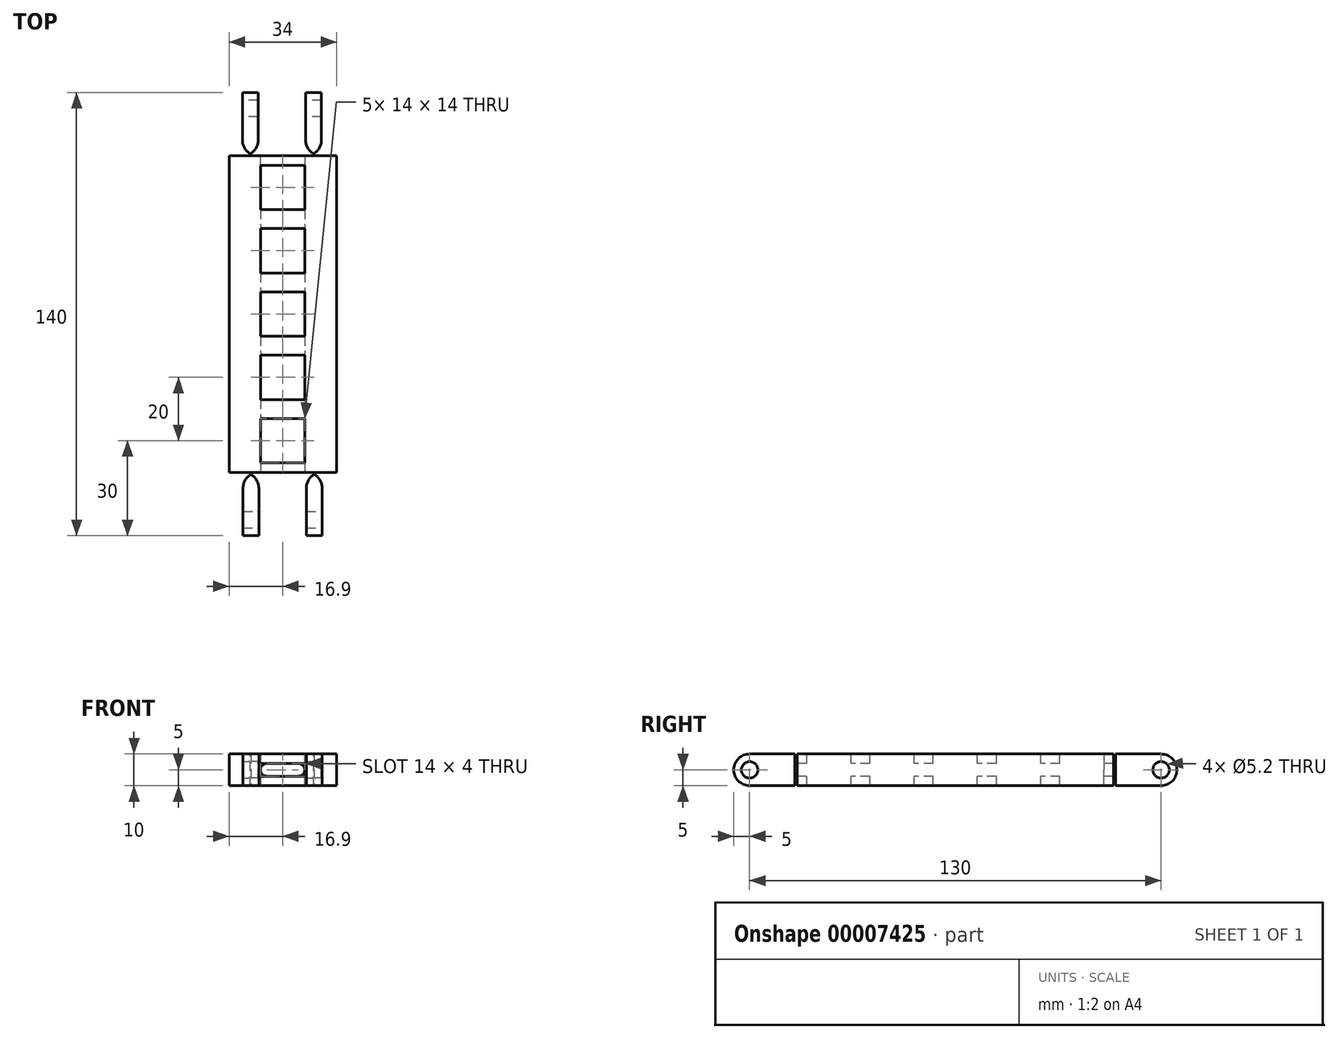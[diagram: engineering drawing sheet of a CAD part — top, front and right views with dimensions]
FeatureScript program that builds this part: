
annotation { "Feature Type Name" : "Feature", "Feature Type Description" : "" }
export const myFeature = defineFeature(function(context is Context, id is Id, definition is map)
    precondition{}
    {
        {
            var Q0;
            Q0=qCreatedBy(makeId("Top.planeOp"),FACE);
            var sketch = newSketch(context, id + "F0", { "sketchPlane" : qUnion([Q0])});
            skLineSegment(sketch, "E0.rect.bottom", {"start": v(17, 50) * mm, "end": v(-17, 50) * mm});
            skLineSegment(sketch, "E0.rect.top", {"start": v(17, -50) * mm, "end": v(-17, -50) * mm});
            skLineSegment(sketch, "E0.rect.left", {"start": v(17, 50) * mm, "end": v(17, -50) * mm});
            skLineSegment(sketch, "E0.rect.right", {"start": v(-17, 50) * mm, "end": v(-17, -50) * mm});
            skPoint(sketch, "E0.rect.middle", {"position": v(0, 0) * mm});
            skLineSegment(sketch, "E1.0", {"start": v(14, 47) * mm, "end": v(14, -47) * mm});
            skLineSegment(sketch, "E1.1", {"start": v(14, 47) * mm, "end": v(-14, 47) * mm});
            skLineSegment(sketch, "E1.2", {"start": v(-14, 47) * mm, "end": v(-14, -47) * mm});
            skLineSegment(sketch, "E1.3", {"start": v(14, -47) * mm, "end": v(-14, -47) * mm});
            skSolve(sketch);
        }
        {
            var Q0;
            Q0=makeQuery(id+"F0.imprint","IMPRINT",FACE,{"disambiguationData":[TD([[makeQuery(id+"F0.imprint","IMPRINT",EDGE,{"derivedFrom":sQuery(id+"F0.wireOp",EDGE,"E0.rect.bottom")}),1.0]])]});
            extrude(context, id + "F1", {"entities" : qUnion([Q0]), "depth" : 10 * mm});
        }
        {
            var Q0;
            Q0=makeQuery(id+"F1.opExtrude","SWEPT_FACE",FACE,{"disambiguationData":[OSD([sQuery(id+"F0.wireOp",EDGE,"E0.rect.top")])]});
            var sketch = newSketch(context, id + "F2", { "sketchPlane" : qUnion([Q0])});
            skLineSegment(sketch, "E2.bottom", {"start": v(-12.6, 10) * mm, "end": v(-7.6, 10) * mm});
            skLineSegment(sketch, "E2.top", {"start": v(-12.6, 0) * mm, "end": v(-7.6, 0) * mm});
            skLineSegment(sketch, "E2.left", {"start": v(-12.6, 10) * mm, "end": v(-12.6, 0) * mm});
            skLineSegment(sketch, "E2.right", {"start": v(-7.6, 10) * mm, "end": v(-7.6, 0) * mm});
            skLineSegment(sketch, "E3", {"start": v(-17, 5) * mm, "end": v(-12.6, 5) * mm});
            skSolve(sketch);
        }
        {
            var Q0;
            {var subQ4=sQuery(id+"F2.wireOp",EDGE,"E2.bottom");Q0=makeQuery(id+"F2.imprint","IMPRINT",FACE,{"disambiguationData":[TD([[makeQuery(id+"F2.imprint","IMPRINT",EDGE,{"derivedFrom":subQ4}),1.0]])]});}
            var Q1;
            Q1=makeQuery(id+"F2.imprint","IMPRINT",FACE,{"disambiguationData":[TD([[makeQuery(id+"F2.imprint","IMPRINT",EDGE,{"derivedFrom":sQuery(id+"F2.wireOp",EDGE,"91248dbe-fa9f-4d01-a37b-5694f4a21cfa.0.MirrorCS")}),1.0]])]});
            extrude(context, id + "F3", {"entities" : qUnion([Q0, Q1]), "depth" : 15 * mm});
        }
        {
            var Q0;
            Q0=makeQuery(id+"F3.opExtrude","SWEPT_FACE",FACE,{"disambiguationData":[OSD([sQuery(id+"F2.wireOp",EDGE,"E2.right")])]});
            var sketch = newSketch(context, id + "F4", { "sketchPlane" : qUnion([Q0])});
            skCircle(sketch, "E4", {"center": v(-65, 5) * mm, "radius": 5 * mm});
            skSolve(sketch);
        }
        {
            var Q0;
            {var subQ0=sQuery(id+"F2.wireOp",EDGE,"E2.right");var subQ1=makeQuery(id+"F3.opExtrude","CAP_EDGE",EDGE,{"disambiguationData":[OSD([subQ0])],"isStart":false});Q0=makeQuery(id+"F4.imprint","IMPRINT",FACE,{"disambiguationData":[TD([[makeQuery(id+"F4.imprint","IMPRINT",EDGE,{"derivedFrom":subQ1}),-1.0]])]});}
            extrude(context, id + "F5", {"entities" : qUnion([Q0]), "oppositeDirection" : true, "depth" : 5 * mm});
        }
        {
            var Q0;
            Q0=makeQuery(id+"F5.opExtrude","SWEPT_BODY",BODY,{"disambiguationData":[OSD([sQuery(id+"F2.wireOp",EDGE,"E2.right"),sQuery(id+"F4.wireOp",EDGE,"E4")])]});
            var Q1;
            Q1=makeQuery(id+"F3.opExtrude","SWEPT_BODY",BODY,{"disambiguationData":[OSD([sQuery(id+"F2.wireOp",EDGE,"E2.bottom"),sQuery(id+"F2.wireOp",EDGE,"E2.top"),sQuery(id+"F2.wireOp",EDGE,"E2.left"),sQuery(id+"F2.wireOp",EDGE,"E2.right")])]});
            booleanBodies(context, id + "F6", {"operationType" : BooleanOperationType.UNION, "tools" : qUnion([Q0, Q1])});
        }
        {
            var Q0;
            {var subQ0=sQuery(id+"F2.wireOp",EDGE,"E2.right");Q0=makeQuery(id+"F6.opBoolean","MERGE",FACE,{"derivedFrom":[makeQuery(id+"F3.opExtrude","SWEPT_FACE",FACE,{"disambiguationData":[OSD([subQ0])]}),makeQuery(id+"F5.opExtrude","CAP_FACE",FACE,{"disambiguationData":[OSD([subQ0,sQuery(id+"F4.wireOp",EDGE,"E4")])],"isStart":true})]});}
            var sketch = newSketch(context, id + "F7", { "sketchPlane" : qUnion([Q0])});
            skLineSegment(sketch, "E5", {"start": v(-65, 10) * mm, "end": v(-65, 0) * mm});
            skCircle(sketch, "E6", {"center": v(-65, 5) * mm, "radius": 2.6 * mm});
            skSolve(sketch);
        }
        {
            var Q0;
            {var subQ0=sQuery(id+"F7.wireOp",EDGE,"E6");var subQ1=sQuery(id+"F7.wireOp",EDGE,"E5");var subQ3=makeQuery(id+"F7.imprint","INTERSECT",VERTEX,{"disambiguationData":[OD(0.0)],"derivedFrom":[subQ1,subQ0]});Q0=makeQuery(id+"F7.imprint","IMPRINT",FACE,{"disambiguationData":[TD([[makeQuery(id+"F7.imprint","IMPRINT",EDGE,{"disambiguationData":[TD([[subQ3,-1.0]])],"derivedFrom":subQ1}),1.0]])]});}
            var Q1;
            {var subQ0=sQuery(id+"F7.wireOp",EDGE,"E6");var subQ1=sQuery(id+"F7.wireOp",EDGE,"E5");var subQ3=makeQuery(id+"F7.imprint","INTERSECT",VERTEX,{"disambiguationData":[OD(0.0)],"derivedFrom":[subQ1,subQ0]});Q1=makeQuery(id+"F7.imprint","IMPRINT",FACE,{"disambiguationData":[TD([[makeQuery(id+"F7.imprint","IMPRINT",EDGE,{"disambiguationData":[TD([[subQ3,-1.0]])],"derivedFrom":subQ1}),-1.0]])]});}
            extrude(context, id + "F8", {"entities" : qUnion([Q0, Q1]), "operationType" : NewBodyOperationType.REMOVE, "endBound" : BoundingType.THROUGH_ALL, "oppositeDirection" : true, "depth" : 25 * mm});
        }
        {
            var Q0;
            Q0=makeQuery(id+"F5.opExtrude","SWEPT_BODY",BODY,{"disambiguationData":[OSD([sQuery(id+"F2.wireOp",EDGE,"E2.right"),sQuery(id+"F4.wireOp",EDGE,"E4")])]});
            transform(context, id + "F9", {"entities" : qUnion([Q0]), "transformType" : TransformType.TRANSLATION_3D, "dx" : 20 * mm, "dy" : 0 * mm, "dz" : 0 * mm, "makeCopy" : true});
        }
        {
            var Q0;
            Q0=makeQuery(id+"F5.opExtrude","SWEPT_BODY",BODY,{"disambiguationData":[OSD([sQuery(id+"F2.wireOp",EDGE,"E2.right"),sQuery(id+"F4.wireOp",EDGE,"E4")])]});
            var Q1;
            Q1=makeQuery(id+"F9.opPattern","COPY",BODY,{"derivedFrom":makeQuery(id+"F5.opExtrude","SWEPT_BODY",BODY,{"disambiguationData":[OSD([sQuery(id+"F2.wireOp",EDGE,"E2.right"),sQuery(id+"F4.wireOp",EDGE,"E4")])]}),"instanceName":"1"});
            transform(context, id + "F10", {"entities" : qUnion([Q0, Q1]), "transformType" : TransformType.TRANSLATION_3D, "dx" : -25.2 * mm, "dy" : 100 * mm, "dz" : 0 * mm, "makeCopy" : true});
        }
        {
            var Q0;
            Q0=makeQuery(id+"F10.opPattern","COPY",BODY,{"derivedFrom":makeQuery(id+"F5.opExtrude","SWEPT_BODY",BODY,{"disambiguationData":[OSD([sQuery(id+"F2.wireOp",EDGE,"E2.right"),sQuery(id+"F4.wireOp",EDGE,"E4")])]}),"instanceName":"1"});
            var Q1;
            Q1=makeQuery(id+"F10.opPattern","COPY",BODY,{"derivedFrom":makeQuery(id+"F9.opPattern","COPY",BODY,{"derivedFrom":makeQuery(id+"F5.opExtrude","SWEPT_BODY",BODY,{"disambiguationData":[OSD([sQuery(id+"F2.wireOp",EDGE,"E2.right"),sQuery(id+"F4.wireOp",EDGE,"E4")])]}),"instanceName":"1"}),"instanceName":"1"});
            var Q2;
            Q2=makeQuery(id+"F10.opPattern","COPY",EDGE,{"derivedFrom":makeQuery(id+"F9.opPattern","COPY",EDGE,{"derivedFrom":makeQuery(id+"F3.opExtrude","CAP_EDGE",EDGE,{"disambiguationData":[OSD([sQuery(id+"F2.wireOp",EDGE,"E2.right")])],"isStart":true}),"instanceName":"1"}),"instanceName":"1"});
            transform(context, id + "F11", {"entities" : qUnion([Q0, Q1]), "transformType" : TransformType.ROTATION, "transformAxis" : qUnion([Q2]), "angle" : 180 * degree, "makeCopy" : false});
        }
        {
            var Q0;
            Q0=makeQuery(id+"F1.opExtrude","SWEPT_FACE",FACE,{"disambiguationData":[OSD([sQuery(id+"F0.wireOp",EDGE,"E1.2")])]});
            var sketch = newSketch(context, id + "F12", { "sketchPlane" : qUnion([Q0])});
            skPoint(sketch, "E7", {"position": v(30, 10) * mm});
            skPoint(sketch, "E8", {"position": v(10, 10) * mm});
            skPoint(sketch, "E9", {"position": v(-10, 10) * mm});
            skPoint(sketch, "E10", {"position": v(-30, 10) * mm});
            skLineSegment(sketch, "E11", {"start": v(-30, 10) * mm, "end": v(-30, 0) * mm});
            skLineSegment(sketch, "E12", {"start": v(-10, 10) * mm, "end": v(-10, 0) * mm});
            skLineSegment(sketch, "E13", {"start": v(10, 10) * mm, "end": v(10, 0) * mm});
            skLineSegment(sketch, "E14", {"start": v(30, 10) * mm, "end": v(30, 0) * mm});
            skPoint(sketch, "E15", {"position": v(33, 10) * mm});
            skPoint(sketch, "E16", {"position": v(27, 10) * mm});
            skLineSegment(sketch, "E17", {"start": v(27, 10) * mm, "end": v(27, 0) * mm});
            skLineSegment(sketch, "E18", {"start": v(33, 10) * mm, "end": v(33, 0) * mm});
            skPoint(sketch, "E19", {"position": v(13, 10) * mm});
            skPoint(sketch, "E20", {"position": v(7, 10) * mm});
            skPoint(sketch, "E21", {"position": v(-7, 10) * mm});
            skPoint(sketch, "E22", {"position": v(-13, 10) * mm});
            skPoint(sketch, "E23", {"position": v(-27, 10) * mm});
            skPoint(sketch, "E24", {"position": v(-33, 10) * mm});
            skLineSegment(sketch, "E25", {"start": v(13, 10) * mm, "end": v(13, 0) * mm});
            skLineSegment(sketch, "E26", {"start": v(7, 10) * mm, "end": v(7, 0) * mm});
            skLineSegment(sketch, "E27", {"start": v(-7, 10) * mm, "end": v(-7, 0) * mm});
            skLineSegment(sketch, "E28", {"start": v(-13, 10) * mm, "end": v(-13, 0) * mm});
            skLineSegment(sketch, "E29", {"start": v(-27, 10) * mm, "end": v(-27, 0) * mm});
            skLineSegment(sketch, "E30", {"start": v(-33, 10) * mm, "end": v(-33, 0) * mm});
            skSolve(sketch);
        }
        {
            var Q0;
            {var subQ3=sQuery(id+"F12.wireOp",EDGE,"E11");Q0=makeQuery(id+"F12.imprint","IMPRINT",FACE,{"disambiguationData":[TD([[makeQuery(id+"F12.imprint","IMPRINT",EDGE,{"derivedFrom":subQ3}),-1.0]])]});}
            var Q1;
            {var subQ3=sQuery(id+"F12.wireOp",EDGE,"E11");Q1=makeQuery(id+"F12.imprint","IMPRINT",FACE,{"disambiguationData":[TD([[makeQuery(id+"F12.imprint","IMPRINT",EDGE,{"derivedFrom":subQ3}),1.0]])]});}
            var Q2;
            {var subQ3=sQuery(id+"F12.wireOp",EDGE,"E12");Q2=makeQuery(id+"F12.imprint","IMPRINT",FACE,{"disambiguationData":[TD([[makeQuery(id+"F12.imprint","IMPRINT",EDGE,{"derivedFrom":subQ3}),-1.0]])]});}
            var Q3;
            {var subQ3=sQuery(id+"F12.wireOp",EDGE,"E12");Q3=makeQuery(id+"F12.imprint","IMPRINT",FACE,{"disambiguationData":[TD([[makeQuery(id+"F12.imprint","IMPRINT",EDGE,{"derivedFrom":subQ3}),1.0]])]});}
            var Q4;
            {var subQ3=sQuery(id+"F12.wireOp",EDGE,"E13");Q4=makeQuery(id+"F12.imprint","IMPRINT",FACE,{"disambiguationData":[TD([[makeQuery(id+"F12.imprint","IMPRINT",EDGE,{"derivedFrom":subQ3}),-1.0]])]});}
            var Q5;
            {var subQ3=sQuery(id+"F12.wireOp",EDGE,"E13");Q5=makeQuery(id+"F12.imprint","IMPRINT",FACE,{"disambiguationData":[TD([[makeQuery(id+"F12.imprint","IMPRINT",EDGE,{"derivedFrom":subQ3}),1.0]])]});}
            var Q6;
            {var subQ3=sQuery(id+"F12.wireOp",EDGE,"E14");Q6=makeQuery(id+"F12.imprint","IMPRINT",FACE,{"disambiguationData":[TD([[makeQuery(id+"F12.imprint","IMPRINT",EDGE,{"derivedFrom":subQ3}),-1.0]])]});}
            var Q7;
            {var subQ3=sQuery(id+"F12.wireOp",EDGE,"E14");Q7=makeQuery(id+"F12.imprint","IMPRINT",FACE,{"disambiguationData":[TD([[makeQuery(id+"F12.imprint","IMPRINT",EDGE,{"derivedFrom":subQ3}),1.0]])]});}
            extrude(context, id + "F13", {"entities" : qUnion([Q0, Q1, Q2, Q3, Q4, Q5, Q6, Q7]), "operationType" : NewBodyOperationType.ADD, "endBound" : BoundingType.UP_TO_NEXT, "depth" : 25 * mm});
        }
        {
            var Q0;
            {var subQ2=sQuery(id+"F2.wireOp",EDGE,"E2.right");Q0=makeQuery(id+"F2.imprint","IMPRINT",FACE,{"disambiguationData":[TD([[makeQuery(id+"F2.imprint","IMPRINT",EDGE,{"derivedFrom":subQ2}),1.0]])]});}
            var sketch = newSketch(context, id + "F14", { "sketchPlane" : qUnion([Q0])});
            skPoint(sketch, "E31", {"position": v(-7.1, 10) * mm});
            skPoint(sketch, "E32", {"position": v(6.9, 9.98) * mm});
            skLineSegment(sketch, "E33", {"start": v(-7.1, 10) * mm, "end": v(-7.1, 0) * mm});
            skLineSegment(sketch, "E34", {"start": v(6.9, 9.98) * mm, "end": v(6.9, 0) * mm});
            skPoint(sketch, "E35", {"position": v(-7.1, 7) * mm});
            skPoint(sketch, "E36", {"position": v(-7.1, 3) * mm});
            skPoint(sketch, "E37", {"position": v(6.9, 6.98) * mm});
            skPoint(sketch, "E38", {"position": v(6.9, 3) * mm});
            skLineSegment(sketch, "E39.bottom", {"start": v(-7.1, 7) * mm, "end": v(6.9, 7) * mm});
            skLineSegment(sketch, "E39.top", {"start": v(-7.1, 3) * mm, "end": v(6.9, 3) * mm});
            skLineSegment(sketch, "E39.left", {"start": v(-7.1, 7) * mm, "end": v(-7.1, 3) * mm});
            skLineSegment(sketch, "E39.right", {"start": v(6.9, 7) * mm, "end": v(6.9, 3) * mm});
            skSolve(sketch);
        }
        {
            var Q0;
            Q0=makeQuery(id+"F14.imprint","IMPRINT",FACE,{"disambiguationData":[TD([[makeQuery(id+"F14.imprint","IMPRINT",EDGE,{"derivedFrom":sQuery(id+"F14.wireOp",EDGE,"E39.bottom")}),-1.0]])]});
            extrude(context, id + "F15", {"entities" : qUnion([Q0]), "operationType" : NewBodyOperationType.REMOVE, "endBound" : BoundingType.THROUGH_ALL, "oppositeDirection" : true, "depth" : 25 * mm});
        }
        {
            var Q0;
            Q0=makeQuery(id+"F1.opExtrude","SWEPT_FACE",FACE,{"disambiguationData":[OSD([sQuery(id+"F0.wireOp",EDGE,"E1.1")])]});
            var sketch = newSketch(context, id + "F16", { "sketchPlane" : qUnion([Q0])});
            skLineSegment(sketch, "E40", {"start": v(-7.1, 7) * mm, "end": v(-7.1, 10) * mm});
            skLineSegment(sketch, "E41", {"start": v(-7.1, 3) * mm, "end": v(-7.1, 0) * mm});
            skPoint(sketch, "E42", {"position": v(-14.5, 10) * mm});
            skLineSegment(sketch, "E43", {"start": v(-14.5, 10) * mm, "end": v(-14.5, 0) * mm});
            skLineSegment(sketch, "E44", {"start": v(6.9, 7) * mm, "end": v(6.9, 10) * mm});
            skLineSegment(sketch, "E45", {"start": v(6.9, 3) * mm, "end": v(6.9, 0) * mm});
            skPoint(sketch, "E46", {"position": v(14.3, 10) * mm});
            skLineSegment(sketch, "E47", {"start": v(14.3, 10) * mm, "end": v(14.3, 0) * mm});
            skSolve(sketch);
        }
        {
            var Q0;
            {var subQ3=sQuery(id+"F16.wireOp",EDGE,"E40");Q0=makeQuery(id+"F16.imprint","IMPRINT",FACE,{"disambiguationData":[TD([[makeQuery(id+"F16.imprint","IMPRINT",EDGE,{"derivedFrom":subQ3}),1.0]])]});}
            var Q1;
            {var subQ3=sQuery(id+"F16.wireOp",EDGE,"E44");Q1=makeQuery(id+"F16.imprint","IMPRINT",FACE,{"disambiguationData":[TD([[makeQuery(id+"F16.imprint","IMPRINT",EDGE,{"derivedFrom":subQ3}),-1.0]])]});}
            var Q2;
            Q2=makeQuery(id+"F1.opExtrude","SWEPT_BODY",BODY,{"disambiguationData":[OSD([sQuery(id+"F0.wireOp",EDGE,"E0.rect.bottom"),sQuery(id+"F0.wireOp",EDGE,"E0.rect.top"),sQuery(id+"F0.wireOp",EDGE,"E0.rect.left"),sQuery(id+"F0.wireOp",EDGE,"E0.rect.right"),sQuery(id+"F0.wireOp",EDGE,"E1.0"),sQuery(id+"F0.wireOp",EDGE,"E1.1"),sQuery(id+"F0.wireOp",EDGE,"E1.2"),sQuery(id+"F0.wireOp",EDGE,"E1.3")])]});
            extrude(context, id + "F17", {"entities" : qUnion([Q0, Q1]), "operationType" : NewBodyOperationType.ADD, "endBoundEntity" : qUnion([Q2]), "depth" : 95 * mm});
        }
        {
            var Q0;
            Q0=makeQuery(id+"F3.opExtrude","CAP_EDGE",EDGE,{"disambiguationData":[OSD([sQuery(id+"F2.wireOp",EDGE,"E2.left")])],"isStart":true});
            var Q1;
            Q1=makeQuery(id+"F3.opExtrude","CAP_EDGE",EDGE,{"disambiguationData":[OSD([sQuery(id+"F2.wireOp",EDGE,"E2.right")])],"isStart":true});
            var Q2;
            Q2=makeQuery(id+"F9.opPattern","COPY",EDGE,{"derivedFrom":makeQuery(id+"F3.opExtrude","CAP_EDGE",EDGE,{"disambiguationData":[OSD([sQuery(id+"F2.wireOp",EDGE,"E2.left")])],"isStart":true}),"instanceName":"1"});
            var Q3;
            Q3=makeQuery(id+"F9.opPattern","COPY",EDGE,{"derivedFrom":makeQuery(id+"F3.opExtrude","CAP_EDGE",EDGE,{"disambiguationData":[OSD([sQuery(id+"F2.wireOp",EDGE,"E2.right")])],"isStart":true}),"instanceName":"1"});
            var Q4;
            Q4=makeQuery(id+"F10.opPattern","COPY",EDGE,{"derivedFrom":makeQuery(id+"F9.opPattern","COPY",EDGE,{"derivedFrom":makeQuery(id+"F3.opExtrude","CAP_EDGE",EDGE,{"disambiguationData":[OSD([sQuery(id+"F2.wireOp",EDGE,"E2.right")])],"isStart":true}),"instanceName":"1"}),"instanceName":"1"});
            var Q5;
            Q5=makeQuery(id+"F10.opPattern","COPY",EDGE,{"derivedFrom":makeQuery(id+"F3.opExtrude","CAP_EDGE",EDGE,{"disambiguationData":[OSD([sQuery(id+"F2.wireOp",EDGE,"E2.right")])],"isStart":true}),"instanceName":"1"});
            var Q6;
            Q6=makeQuery(id+"F10.opPattern","COPY",EDGE,{"derivedFrom":makeQuery(id+"F9.opPattern","COPY",EDGE,{"derivedFrom":makeQuery(id+"F3.opExtrude","CAP_EDGE",EDGE,{"disambiguationData":[OSD([sQuery(id+"F2.wireOp",EDGE,"E2.left")])],"isStart":true}),"instanceName":"1"}),"instanceName":"1"});
            var Q7;
            Q7=makeQuery(id+"F10.opPattern","COPY",EDGE,{"derivedFrom":makeQuery(id+"F3.opExtrude","CAP_EDGE",EDGE,{"disambiguationData":[OSD([sQuery(id+"F2.wireOp",EDGE,"E2.left")])],"isStart":true}),"instanceName":"1"});
            fillet(context, id + "F18", {"entities" : qUnion([Q0, Q1, Q2, Q3, Q4, Q5, Q6, Q7]), "radius" : 5 * mm, "tangentPropagation" : true, "allowEdgeOverflow" : false});
        }
        {
            var Q0;
            Q0=makeQuery(id+"F15.boolean.opBoolean","COPY",EDGE,{"disambiguationData":[OD(5.0)],"derivedFrom":makeQuery(id+"F15.opExtrude","SWEPT_EDGE",EDGE,{"disambiguationData":[OSD([sQuery(id+"F14.wireOp",EDGE,"E33"),sQuery(id+"F14.wireOp",EDGE,"E39.top"),sQuery(id+"F14.wireOp",EDGE,"E39.left")])]})});
            var Q1;
            Q1=makeQuery(id+"F15.boolean.opBoolean","COPY",EDGE,{"disambiguationData":[OD(0.0)],"derivedFrom":makeQuery(id+"F15.opExtrude","SWEPT_EDGE",EDGE,{"disambiguationData":[OSD([sQuery(id+"F14.wireOp",EDGE,"E33"),sQuery(id+"F14.wireOp",EDGE,"E39.top"),sQuery(id+"F14.wireOp",EDGE,"E39.left")])]})});
            var Q2;
            Q2=makeQuery(id+"F15.boolean.opBoolean","COPY",EDGE,{"disambiguationData":[OD(4.0)],"derivedFrom":makeQuery(id+"F15.opExtrude","SWEPT_EDGE",EDGE,{"disambiguationData":[OSD([sQuery(id+"F14.wireOp",EDGE,"E33"),sQuery(id+"F14.wireOp",EDGE,"E39.top"),sQuery(id+"F14.wireOp",EDGE,"E39.left")])]})});
            var Q3;
            Q3=makeQuery(id+"F15.boolean.opBoolean","COPY",EDGE,{"disambiguationData":[OD(3.0)],"derivedFrom":makeQuery(id+"F15.opExtrude","SWEPT_EDGE",EDGE,{"disambiguationData":[OSD([sQuery(id+"F14.wireOp",EDGE,"E33"),sQuery(id+"F14.wireOp",EDGE,"E39.top"),sQuery(id+"F14.wireOp",EDGE,"E39.left")])]})});
            var Q4;
            Q4=makeQuery(id+"F15.boolean.opBoolean","COPY",EDGE,{"disambiguationData":[OD(2.0)],"derivedFrom":makeQuery(id+"F15.opExtrude","SWEPT_EDGE",EDGE,{"disambiguationData":[OSD([sQuery(id+"F14.wireOp",EDGE,"E33"),sQuery(id+"F14.wireOp",EDGE,"E39.top"),sQuery(id+"F14.wireOp",EDGE,"E39.left")])]})});
            var Q5;
            Q5=makeQuery(id+"F15.boolean.opBoolean","COPY",EDGE,{"disambiguationData":[OD(1.0)],"derivedFrom":makeQuery(id+"F15.opExtrude","SWEPT_EDGE",EDGE,{"disambiguationData":[OSD([sQuery(id+"F14.wireOp",EDGE,"E33"),sQuery(id+"F14.wireOp",EDGE,"E39.top"),sQuery(id+"F14.wireOp",EDGE,"E39.left")])]})});
            var Q6;
            Q6=makeQuery(id+"F15.boolean.opBoolean","COPY",EDGE,{"disambiguationData":[OD(1.0)],"derivedFrom":makeQuery(id+"F15.opExtrude","SWEPT_EDGE",EDGE,{"disambiguationData":[OSD([sQuery(id+"F14.wireOp",EDGE,"E34"),sQuery(id+"F14.wireOp",EDGE,"E39.top"),sQuery(id+"F14.wireOp",EDGE,"E39.right")])]})});
            var Q7;
            Q7=makeQuery(id+"F15.boolean.opBoolean","COPY",EDGE,{"disambiguationData":[OD(2.0)],"derivedFrom":makeQuery(id+"F15.opExtrude","SWEPT_EDGE",EDGE,{"disambiguationData":[OSD([sQuery(id+"F14.wireOp",EDGE,"E34"),sQuery(id+"F14.wireOp",EDGE,"E39.top"),sQuery(id+"F14.wireOp",EDGE,"E39.right")])]})});
            var Q8;
            Q8=makeQuery(id+"F15.boolean.opBoolean","COPY",EDGE,{"disambiguationData":[OD(3.0)],"derivedFrom":makeQuery(id+"F15.opExtrude","SWEPT_EDGE",EDGE,{"disambiguationData":[OSD([sQuery(id+"F14.wireOp",EDGE,"E34"),sQuery(id+"F14.wireOp",EDGE,"E39.top"),sQuery(id+"F14.wireOp",EDGE,"E39.right")])]})});
            var Q9;
            Q9=makeQuery(id+"F15.boolean.opBoolean","COPY",EDGE,{"disambiguationData":[OD(4.0)],"derivedFrom":makeQuery(id+"F15.opExtrude","SWEPT_EDGE",EDGE,{"disambiguationData":[OSD([sQuery(id+"F14.wireOp",EDGE,"E34"),sQuery(id+"F14.wireOp",EDGE,"E39.top"),sQuery(id+"F14.wireOp",EDGE,"E39.right")])]})});
            var Q10;
            Q10=makeQuery(id+"F15.boolean.opBoolean","COPY",EDGE,{"disambiguationData":[OD(5.0)],"derivedFrom":makeQuery(id+"F15.opExtrude","SWEPT_EDGE",EDGE,{"disambiguationData":[OSD([sQuery(id+"F14.wireOp",EDGE,"E34"),sQuery(id+"F14.wireOp",EDGE,"E39.top"),sQuery(id+"F14.wireOp",EDGE,"E39.right")])]})});
            var Q11;
            Q11=makeQuery(id+"F15.boolean.opBoolean","COPY",EDGE,{"disambiguationData":[OD(0.0)],"derivedFrom":makeQuery(id+"F15.opExtrude","SWEPT_EDGE",EDGE,{"disambiguationData":[OSD([sQuery(id+"F14.wireOp",EDGE,"E34"),sQuery(id+"F14.wireOp",EDGE,"E39.top"),sQuery(id+"F14.wireOp",EDGE,"E39.right")])]})});
            var Q12;
            Q12=makeQuery(id+"F15.boolean.opBoolean","COPY",EDGE,{"disambiguationData":[OD(0.0)],"derivedFrom":makeQuery(id+"F15.opExtrude","SWEPT_EDGE",EDGE,{"disambiguationData":[OSD([sQuery(id+"F14.wireOp",EDGE,"E39.bottom"),sQuery(id+"F14.wireOp",EDGE,"E39.right")])]})});
            var Q13;
            Q13=makeQuery(id+"F15.boolean.opBoolean","COPY",EDGE,{"disambiguationData":[OD(5.0)],"derivedFrom":makeQuery(id+"F15.opExtrude","SWEPT_EDGE",EDGE,{"disambiguationData":[OSD([sQuery(id+"F14.wireOp",EDGE,"E39.bottom"),sQuery(id+"F14.wireOp",EDGE,"E39.right")])]})});
            var Q14;
            Q14=makeQuery(id+"F15.boolean.opBoolean","COPY",EDGE,{"disambiguationData":[OD(4.0)],"derivedFrom":makeQuery(id+"F15.opExtrude","SWEPT_EDGE",EDGE,{"disambiguationData":[OSD([sQuery(id+"F14.wireOp",EDGE,"E39.bottom"),sQuery(id+"F14.wireOp",EDGE,"E39.right")])]})});
            var Q15;
            Q15=makeQuery(id+"F15.boolean.opBoolean","COPY",EDGE,{"disambiguationData":[OD(3.0)],"derivedFrom":makeQuery(id+"F15.opExtrude","SWEPT_EDGE",EDGE,{"disambiguationData":[OSD([sQuery(id+"F14.wireOp",EDGE,"E39.bottom"),sQuery(id+"F14.wireOp",EDGE,"E39.right")])]})});
            var Q16;
            Q16=makeQuery(id+"F15.boolean.opBoolean","COPY",EDGE,{"disambiguationData":[OD(2.0)],"derivedFrom":makeQuery(id+"F15.opExtrude","SWEPT_EDGE",EDGE,{"disambiguationData":[OSD([sQuery(id+"F14.wireOp",EDGE,"E39.bottom"),sQuery(id+"F14.wireOp",EDGE,"E39.right")])]})});
            var Q17;
            Q17=makeQuery(id+"F15.boolean.opBoolean","COPY",EDGE,{"disambiguationData":[OD(1.0)],"derivedFrom":makeQuery(id+"F15.opExtrude","SWEPT_EDGE",EDGE,{"disambiguationData":[OSD([sQuery(id+"F14.wireOp",EDGE,"E39.bottom"),sQuery(id+"F14.wireOp",EDGE,"E39.right")])]})});
            var Q18;
            Q18=makeQuery(id+"F15.boolean.opBoolean","COPY",EDGE,{"disambiguationData":[OD(1.0)],"derivedFrom":makeQuery(id+"F15.opExtrude","SWEPT_EDGE",EDGE,{"disambiguationData":[OSD([sQuery(id+"F14.wireOp",EDGE,"E33"),sQuery(id+"F14.wireOp",EDGE,"E39.bottom"),sQuery(id+"F14.wireOp",EDGE,"E39.left")])]})});
            var Q19;
            Q19=makeQuery(id+"F15.boolean.opBoolean","COPY",EDGE,{"disambiguationData":[OD(2.0)],"derivedFrom":makeQuery(id+"F15.opExtrude","SWEPT_EDGE",EDGE,{"disambiguationData":[OSD([sQuery(id+"F14.wireOp",EDGE,"E33"),sQuery(id+"F14.wireOp",EDGE,"E39.bottom"),sQuery(id+"F14.wireOp",EDGE,"E39.left")])]})});
            var Q20;
            Q20=makeQuery(id+"F15.boolean.opBoolean","COPY",EDGE,{"disambiguationData":[OD(3.0)],"derivedFrom":makeQuery(id+"F15.opExtrude","SWEPT_EDGE",EDGE,{"disambiguationData":[OSD([sQuery(id+"F14.wireOp",EDGE,"E33"),sQuery(id+"F14.wireOp",EDGE,"E39.bottom"),sQuery(id+"F14.wireOp",EDGE,"E39.left")])]})});
            var Q21;
            Q21=makeQuery(id+"F15.boolean.opBoolean","COPY",EDGE,{"disambiguationData":[OD(4.0)],"derivedFrom":makeQuery(id+"F15.opExtrude","SWEPT_EDGE",EDGE,{"disambiguationData":[OSD([sQuery(id+"F14.wireOp",EDGE,"E33"),sQuery(id+"F14.wireOp",EDGE,"E39.bottom"),sQuery(id+"F14.wireOp",EDGE,"E39.left")])]})});
            var Q22;
            Q22=makeQuery(id+"F15.boolean.opBoolean","COPY",EDGE,{"disambiguationData":[OD(5.0)],"derivedFrom":makeQuery(id+"F15.opExtrude","SWEPT_EDGE",EDGE,{"disambiguationData":[OSD([sQuery(id+"F14.wireOp",EDGE,"E33"),sQuery(id+"F14.wireOp",EDGE,"E39.bottom"),sQuery(id+"F14.wireOp",EDGE,"E39.left")])]})});
            var Q23;
            Q23=makeQuery(id+"F15.boolean.opBoolean","COPY",EDGE,{"disambiguationData":[OD(0.0)],"derivedFrom":makeQuery(id+"F15.opExtrude","SWEPT_EDGE",EDGE,{"disambiguationData":[OSD([sQuery(id+"F14.wireOp",EDGE,"E33"),sQuery(id+"F14.wireOp",EDGE,"E39.bottom"),sQuery(id+"F14.wireOp",EDGE,"E39.left")])]})});
            fillet(context, id + "F19", {"entities" : qUnion([Q0, Q1, Q2, Q3, Q4, Q5, Q6, Q7, Q8, Q9, Q10, Q11, Q12, Q13, Q14, Q15, Q16, Q17, Q18, Q19, Q20, Q21, Q22, Q23]), "radius" : 2 * mm, "tangentPropagation" : true, "allowEdgeOverflow" : false});
        }
    });
